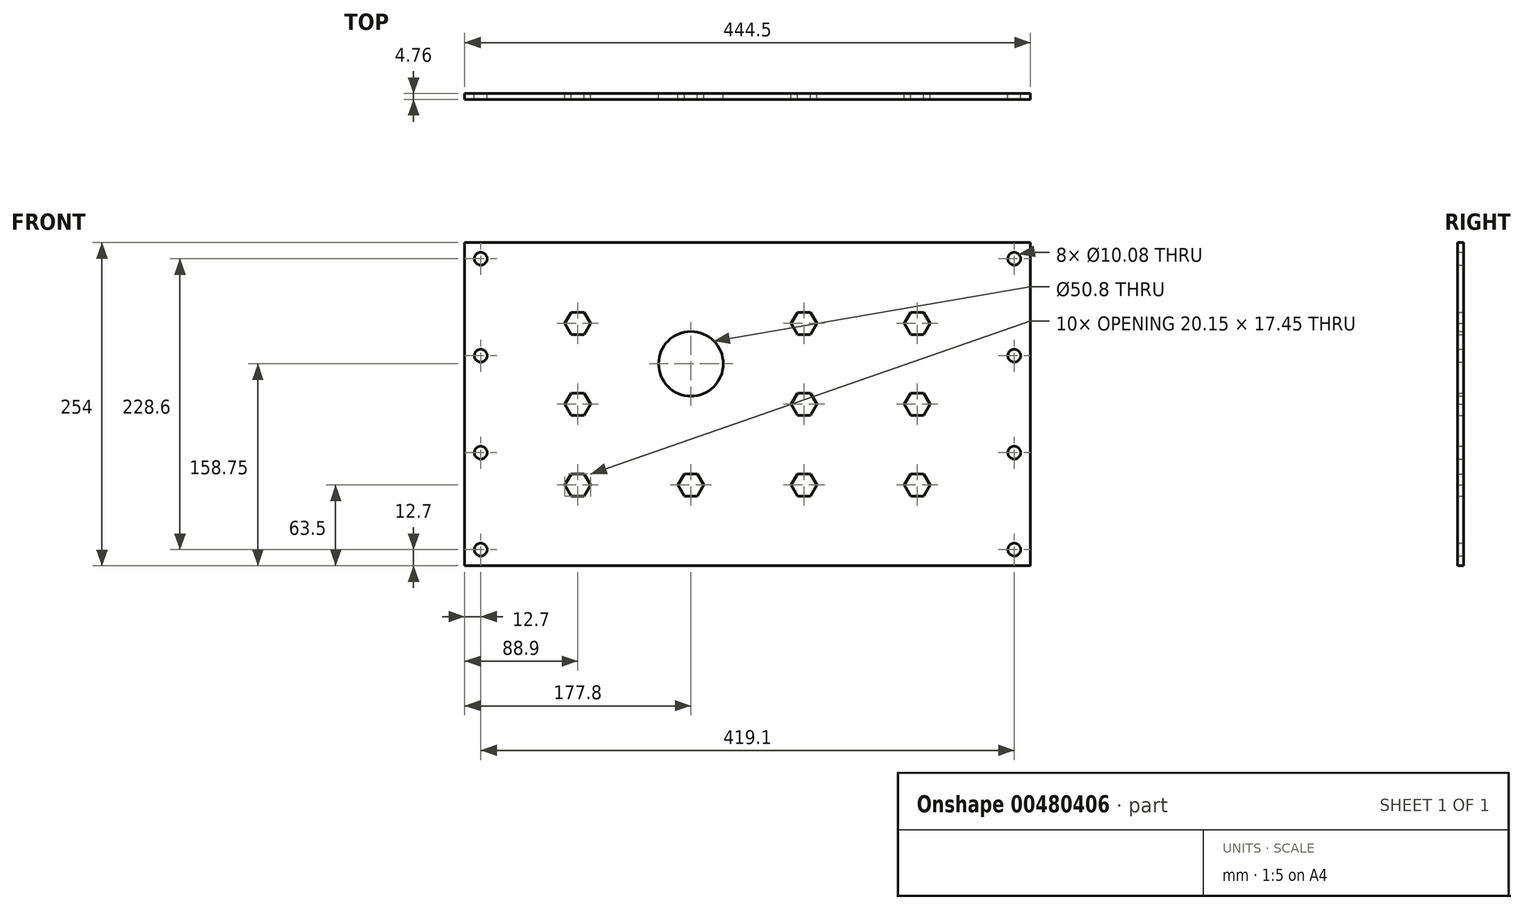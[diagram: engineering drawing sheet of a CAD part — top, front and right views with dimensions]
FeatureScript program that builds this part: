
annotation { "Feature Type Name" : "Feature", "Feature Type Description" : "" }
export const myFeature = defineFeature(function(context is Context, id is Id, definition is map)
    precondition{}
    {
        {
            var Q0;
            Q0=qCreatedBy(makeId("Front.planeOp"),FACE);
            var sketch = newSketch(context, id + "F0", { "sketchPlane" : qUnion([Q0])});
            skLineSegment(sketch, "E0.bottom", {"start": v(-222.25, 127) * mm, "end": v(222.25, 127) * mm});
            skLineSegment(sketch, "E0.top", {"start": v(-222.25, -127) * mm, "end": v(222.25, -127) * mm});
            skLineSegment(sketch, "E0.left", {"start": v(-222.25, 127) * mm, "end": v(-222.25, -127) * mm});
            skLineSegment(sketch, "E0.right", {"start": v(222.25, 127) * mm, "end": v(222.25, -127) * mm});
            skPoint(sketch, "E0.middle", {"position": v(0, 0) * mm});
            skCircle(sketch, "E1.cCircle", {"center": v(-133.35, 63.5) * mm, "radius": 8.72 * mm, "construction": true});
            skLineSegment(sketch, "E1.0", {"start": v(-138.39, 72.22) * mm, "end": v(-128.31, 72.22) * mm});
            skLineSegment(sketch, "E1.1", {"start": v(-128.31, 72.22) * mm, "end": v(-123.28, 63.5) * mm});
            skLineSegment(sketch, "E1.2", {"start": v(-123.28, 63.5) * mm, "end": v(-128.31, 54.78) * mm});
            skLineSegment(sketch, "E1.3", {"start": v(-128.31, 54.78) * mm, "end": v(-138.39, 54.78) * mm});
            skLineSegment(sketch, "E1.4", {"start": v(-138.39, 54.78) * mm, "end": v(-143.42, 63.5) * mm});
            skLineSegment(sketch, "E1.5", {"start": v(-143.42, 63.5) * mm, "end": v(-138.39, 72.22) * mm});
            skPoint(sketch, "E1.0.midPoint", {"position": v(-133.35, 72.22) * mm});
            skCircle(sketch, "E2.cCircle", {"center": v(-133.35, 0) * mm, "radius": 8.72 * mm, "construction": true});
            skLineSegment(sketch, "E2.0", {"start": v(-138.39, 8.72) * mm, "end": v(-128.31, 8.72) * mm});
            skLineSegment(sketch, "E2.1", {"start": v(-128.31, 8.72) * mm, "end": v(-123.28, 0) * mm});
            skLineSegment(sketch, "E2.2", {"start": v(-123.28, 0) * mm, "end": v(-128.31, -8.72) * mm});
            skLineSegment(sketch, "E2.3", {"start": v(-128.31, -8.72) * mm, "end": v(-138.39, -8.72) * mm});
            skLineSegment(sketch, "E2.4", {"start": v(-138.39, -8.72) * mm, "end": v(-143.42, 0) * mm});
            skLineSegment(sketch, "E2.5", {"start": v(-143.42, 0) * mm, "end": v(-138.39, 8.72) * mm});
            skPoint(sketch, "E2.0.midPoint", {"position": v(-133.35, 8.72) * mm});
            skCircle(sketch, "E3.cCircle", {"center": v(-133.35, -63.5) * mm, "radius": 8.72 * mm, "construction": true});
            skLineSegment(sketch, "E3.0", {"start": v(-138.39, -54.78) * mm, "end": v(-128.31, -54.78) * mm});
            skLineSegment(sketch, "E3.1", {"start": v(-128.31, -54.78) * mm, "end": v(-123.28, -63.5) * mm});
            skLineSegment(sketch, "E3.2", {"start": v(-123.28, -63.5) * mm, "end": v(-128.31, -72.22) * mm});
            skLineSegment(sketch, "E3.3", {"start": v(-128.31, -72.22) * mm, "end": v(-138.39, -72.22) * mm});
            skLineSegment(sketch, "E3.4", {"start": v(-138.39, -72.22) * mm, "end": v(-143.42, -63.5) * mm});
            skLineSegment(sketch, "E3.5", {"start": v(-143.42, -63.5) * mm, "end": v(-138.39, -54.78) * mm});
            skPoint(sketch, "E3.0.midPoint", {"position": v(-133.35, -54.78) * mm});
            skCircle(sketch, "E4.cCircle", {"center": v(133.35, 63.5) * mm, "radius": 8.72 * mm, "construction": true});
            skLineSegment(sketch, "E4.0", {"start": v(128.31, 72.22) * mm, "end": v(138.39, 72.22) * mm});
            skLineSegment(sketch, "E4.1", {"start": v(138.39, 72.22) * mm, "end": v(143.42, 63.5) * mm});
            skLineSegment(sketch, "E4.2", {"start": v(143.42, 63.5) * mm, "end": v(138.39, 54.78) * mm});
            skLineSegment(sketch, "E4.3", {"start": v(138.39, 54.78) * mm, "end": v(128.31, 54.78) * mm});
            skLineSegment(sketch, "E4.4", {"start": v(128.31, 54.78) * mm, "end": v(123.28, 63.5) * mm});
            skLineSegment(sketch, "E4.5", {"start": v(123.28, 63.5) * mm, "end": v(128.31, 72.22) * mm});
            skPoint(sketch, "E4.0.midPoint", {"position": v(133.35, 72.22) * mm});
            skCircle(sketch, "E5.cCircle", {"center": v(133.35, 0) * mm, "radius": 8.72 * mm, "construction": true});
            skPoint(sketch, "E5.cCircle.centerSnap0", {"position": v(133.35, 54.78) * mm});
            skLineSegment(sketch, "E5.0", {"start": v(128.31, 8.72) * mm, "end": v(138.39, 8.72) * mm});
            skLineSegment(sketch, "E5.1", {"start": v(138.39, 8.72) * mm, "end": v(143.42, 0) * mm});
            skLineSegment(sketch, "E5.2", {"start": v(143.42, 0) * mm, "end": v(138.39, -8.72) * mm});
            skLineSegment(sketch, "E5.3", {"start": v(138.39, -8.72) * mm, "end": v(128.31, -8.72) * mm});
            skLineSegment(sketch, "E5.4", {"start": v(128.31, -8.72) * mm, "end": v(123.28, 0) * mm});
            skLineSegment(sketch, "E5.5", {"start": v(123.28, 0) * mm, "end": v(128.31, 8.72) * mm});
            skPoint(sketch, "E5.0.midPoint", {"position": v(133.35, 8.72) * mm});
            skCircle(sketch, "E6.cCircle", {"center": v(133.35, -63.5) * mm, "radius": 8.72 * mm, "construction": true});
            skLineSegment(sketch, "E6.0", {"start": v(128.31, -54.78) * mm, "end": v(138.39, -54.78) * mm});
            skLineSegment(sketch, "E6.1", {"start": v(138.39, -54.78) * mm, "end": v(143.42, -63.5) * mm});
            skLineSegment(sketch, "E6.2", {"start": v(143.42, -63.5) * mm, "end": v(138.39, -72.22) * mm});
            skLineSegment(sketch, "E6.3", {"start": v(138.39, -72.22) * mm, "end": v(128.31, -72.22) * mm});
            skLineSegment(sketch, "E6.4", {"start": v(128.31, -72.22) * mm, "end": v(123.28, -63.5) * mm});
            skLineSegment(sketch, "E6.5", {"start": v(123.28, -63.5) * mm, "end": v(128.31, -54.78) * mm});
            skPoint(sketch, "E6.0.midPoint", {"position": v(133.35, -54.78) * mm});
            skCircle(sketch, "E7.cCircle", {"center": v(44.45, -63.5) * mm, "radius": 8.72 * mm, "construction": true});
            skLineSegment(sketch, "E7.0", {"start": v(39.41, -54.78) * mm, "end": v(49.49, -54.78) * mm});
            skLineSegment(sketch, "E7.1", {"start": v(49.49, -54.78) * mm, "end": v(54.52, -63.5) * mm});
            skLineSegment(sketch, "E7.2", {"start": v(54.52, -63.5) * mm, "end": v(49.49, -72.22) * mm});
            skLineSegment(sketch, "E7.3", {"start": v(49.49, -72.22) * mm, "end": v(39.41, -72.22) * mm});
            skLineSegment(sketch, "E7.4", {"start": v(39.41, -72.22) * mm, "end": v(34.38, -63.5) * mm});
            skLineSegment(sketch, "E7.5", {"start": v(34.38, -63.5) * mm, "end": v(39.41, -54.78) * mm});
            skPoint(sketch, "E7.0.midPoint", {"position": v(44.45, -54.78) * mm});
            skCircle(sketch, "E8.cCircle", {"center": v(44.45, 0) * mm, "radius": 8.72 * mm, "construction": true});
            skLineSegment(sketch, "E8.0", {"start": v(39.41, 8.72) * mm, "end": v(49.49, 8.72) * mm});
            skLineSegment(sketch, "E8.1", {"start": v(49.49, 8.72) * mm, "end": v(54.52, 0) * mm});
            skLineSegment(sketch, "E8.2", {"start": v(54.52, 0) * mm, "end": v(49.49, -8.72) * mm});
            skLineSegment(sketch, "E8.3", {"start": v(49.49, -8.72) * mm, "end": v(39.41, -8.72) * mm});
            skLineSegment(sketch, "E8.4", {"start": v(39.41, -8.72) * mm, "end": v(34.38, 0) * mm});
            skLineSegment(sketch, "E8.5", {"start": v(34.38, 0) * mm, "end": v(39.41, 8.72) * mm});
            skPoint(sketch, "E8.0.midPoint", {"position": v(44.45, 8.72) * mm});
            skCircle(sketch, "E9.cCircle", {"center": v(44.45, 63.5) * mm, "radius": 8.72 * mm, "construction": true});
            skLineSegment(sketch, "E9.0", {"start": v(39.41, 72.22) * mm, "end": v(49.49, 72.22) * mm});
            skLineSegment(sketch, "E9.1", {"start": v(49.49, 72.22) * mm, "end": v(54.52, 63.5) * mm});
            skLineSegment(sketch, "E9.2", {"start": v(54.52, 63.5) * mm, "end": v(49.49, 54.78) * mm});
            skLineSegment(sketch, "E9.3", {"start": v(49.49, 54.78) * mm, "end": v(39.41, 54.78) * mm});
            skLineSegment(sketch, "E9.4", {"start": v(39.41, 54.78) * mm, "end": v(34.38, 63.5) * mm});
            skLineSegment(sketch, "E9.5", {"start": v(34.38, 63.5) * mm, "end": v(39.41, 72.22) * mm});
            skPoint(sketch, "E9.0.midPoint", {"position": v(44.45, 72.22) * mm});
            skCircle(sketch, "E10.cCircle", {"center": v(-44.45, -63.5) * mm, "radius": 8.72 * mm, "construction": true});
            skLineSegment(sketch, "E10.0", {"start": v(-49.49, -54.78) * mm, "end": v(-39.41, -54.78) * mm});
            skLineSegment(sketch, "E10.1", {"start": v(-39.41, -54.78) * mm, "end": v(-34.38, -63.5) * mm});
            skLineSegment(sketch, "E10.2", {"start": v(-34.38, -63.5) * mm, "end": v(-39.41, -72.22) * mm});
            skLineSegment(sketch, "E10.3", {"start": v(-39.41, -72.22) * mm, "end": v(-49.49, -72.22) * mm});
            skLineSegment(sketch, "E10.4", {"start": v(-49.49, -72.22) * mm, "end": v(-54.52, -63.5) * mm});
            skLineSegment(sketch, "E10.5", {"start": v(-54.52, -63.5) * mm, "end": v(-49.49, -54.78) * mm});
            skPoint(sketch, "E10.0.midPoint", {"position": v(-44.45, -54.78) * mm});
            skCircle(sketch, "E11", {"center": v(-44.45, 31.75) * mm, "radius": 25.4 * mm});
            skCircle(sketch, "E12", {"center": v(209.55, 114.3) * mm, "radius": 5.04 * mm});
            skCircle(sketch, "E13", {"center": v(209.55, 38.1) * mm, "radius": 5.04 * mm});
            skCircle(sketch, "E14", {"center": v(209.55, -38.1) * mm, "radius": 5.04 * mm});
            skCircle(sketch, "E15", {"center": v(209.55, -114.3) * mm, "radius": 5.04 * mm});
            skCircle(sketch, "E16", {"center": v(-209.55, 114.3) * mm, "radius": 5.04 * mm});
            skCircle(sketch, "E17", {"center": v(-209.55, 38.1) * mm, "radius": 5.04 * mm});
            skCircle(sketch, "E18", {"center": v(-209.55, -38.1) * mm, "radius": 5.04 * mm});
            skCircle(sketch, "E19", {"center": v(-209.55, -114.3) * mm, "radius": 5.04 * mm});
            skSolve(sketch);
        }
        {
            var Q0;
            Q0 = qSketchRegion(id + "F0", true);
            extrude(context, id + "F1", {"entities" : qUnion([Q0]), "depth" : 4.76 * mm});
        }
    });
